FCSTD DOCUMENT  (FreeCAD 0.18.4R)
Label: keystone_3024_fp
License: Creative Commons Attribution
LicenseURL: http://creativecommons.org/licenses/by/4.0/
objects: Sketcher::SketchObject×4, App::Annotation×2
note: 4 computed .brp shape members not serialized (recipe doc carries the construction recipe); baked Part::Feature solids carry a one-line shape summary decoded from their .brp

FEATURE [App::Annotation] Text  label="Ref#_1.0mm"
  LabelText = REF**
  Position = (-9,-16,0)
FEATURE [App::Annotation] Text001  label="Value#_0.8mm"
  LabelText = Value 
  Position = (8,-16,0)
FEATURE [Sketcher::SketchObject] Sketch  label="F_Silks_0.16"
  sketch-geometry (57):
    g0: ArcOfCircle CenterX=6.39178 CenterY=-6.2773 CenterZ=0 NormalX=0 NormalY=0 NormalZ=1 AngleXU=0 Radius=2.3622 StartAngle=5.5152 EndAngle=6.28319
    g1: ArcOfCircle CenterX=6.39178 CenterY=6.27729 CenterZ=0 NormalX=0 NormalY=0 NormalZ=1 AngleXU=-3.14159 Radius=2.3622 StartAngle=2.48526 EndAngle=3.14159
    g2: LineSegment StartX=-2.54 StartY=-11.6713 StartZ=0 EndX=2.54 EndY=-11.6713 EndZ=0
    g3: LineSegment StartX=4.7117 StartY=-11.6713 StartZ=0 EndX=2.54 EndY=-11.6713 EndZ=0
    g4: LineSegment StartX=-2.54 StartY=-11.6713 StartZ=0 EndX=-4.7117 EndY=-11.6713 EndZ=0
    g5: LineSegment StartX=2.54 StartY=11.6713 StartZ=0 EndX=-2.54 EndY=11.6713 EndZ=0
    g6: LineSegment StartX=-2.54 StartY=11.6713 StartZ=0 EndX=-4.7117 EndY=11.6713 EndZ=0
    g7: LineSegment StartX=4.7117 StartY=11.6713 StartZ=0 EndX=2.54 EndY=11.6713 EndZ=0
    g8: LineSegment StartX=-11.5443 StartY=3.7846 StartZ=0 EndX=-4.7117 EndY=11.4173 EndZ=0
    g9: LineSegment StartX=-4.7117 StartY=-11.4173 StartZ=0 EndX=-11.5443 EndY=-3.7846 EndZ=0
    g10: LineSegment StartX=8.09093 StartY=-7.91829 StartZ=0 EndX=4.7117 EndY=-11.4173 EndZ=0
    g11: ArcOfCircle CenterX=6.39178 CenterY=-6.2773 CenterZ=0 NormalX=0 NormalY=0 NormalZ=1 AngleXU=0 Radius=2.3622 StartAngle=0 EndAngle=0.656334
    g12: ArcOfCircle CenterX=6.39178 CenterY=6.27729 CenterZ=0 NormalX=0 NormalY=0 NormalZ=1 AngleXU=-3.14159 Radius=2.3622 StartAngle=3.14159 EndAngle=3.90958
    g13: LineSegment StartX=4.7117 StartY=11.4173 StartZ=0 EndX=8.09093 EndY=7.91828 EndZ=0
    g14: BSplineCurve PolesCount=15 KnotsCount=15 Degree=1 IsPeriodic=0
    g15: BSplineCurve PolesCount=15 KnotsCount=15 Degree=1 IsPeriodic=0
    g16: LineSegment StartX=-12.0523 StartY=-3.7846 StartZ=0 EndX=-11.7983 EndY=-3.7846 EndZ=0
    g17: LineSegment StartX=-12.0523 StartY=3.7846 StartZ=0 EndX=-11.7983 EndY=3.7846 EndZ=0
    g18: LineSegment StartX=-12.0523 StartY=3.7846 StartZ=0 EndX=-12.0523 EndY=-3.7846 EndZ=0
    g19: LineSegment StartX=-11.7983 StartY=3.7846 StartZ=0 EndX=-11.7983 EndY=-3.7846 EndZ=0
    g20: BSplineCurve PolesCount=15 KnotsCount=15 Degree=1 IsPeriodic=0
    g21: BSplineCurve PolesCount=15 KnotsCount=15 Degree=1 IsPeriodic=0
    g22: BSplineCurve PolesCount=15 KnotsCount=15 Degree=1 IsPeriodic=0
    g23: BSplineCurve PolesCount=15 KnotsCount=15 Degree=1 IsPeriodic=0
    g24: LineSegment StartX=-11.5443 StartY=-3.7846 StartZ=0 EndX=-11.5443 EndY=3.7846 EndZ=0
    g25: LineSegment StartX=4.7117 StartY=-11.4173 StartZ=0 EndX=-4.7117 EndY=-11.4173 EndZ=0
    g26: LineSegment StartX=-4.7117 StartY=11.4173 StartZ=0 EndX=4.7117 EndY=11.4173 EndZ=0
    g27: LineSegment StartX=-11.7675 StartY=-3.6322 StartZ=0 EndX=-11.7675 EndY=3.6322 EndZ=0
    g28: LineSegment StartX=-12.0723 StartY=-3.683 StartZ=0 EndX=-12.0723 EndY=3.683 EndZ=0
    g29: LineSegment StartX=-7.43483 StartY=7.10236 StartZ=0 EndX=-10.1203 EndY=4.01304 EndZ=0
    g30: ArcOfCircle CenterX=-5.3921 CenterY=9.2456 CenterZ=0 NormalX=0 NormalY=0 NormalZ=1 AngleXU=0 Radius=2.3622 StartAngle=1.5708 EndAngle=2.35619
    g31: LineSegment StartX=-5.3921 StartY=11.6078 StartZ=0 EndX=4.7425 EndY=11.6078 EndZ=0
    g32: LineSegment StartX=4.7425 StartY=11.6078 StartZ=0 EndX=4.7425 EndY=10.9728 EndZ=0
    g33: LineSegment StartX=3.9297 StartY=10.16 StartZ=0 EndX=-0.725459 EndY=10.16 EndZ=0
    g34: ArcOfCircle CenterX=-0.725459 CenterY=1.27 CenterZ=0 NormalX=0 NormalY=0 NormalZ=1 AngleXU=0 Radius=8.89 StartAngle=1.5708 EndAngle=2.42601
    g35: ArcOfCircle CenterX=-9.5069 CenterY=3.4798 CenterZ=0 NormalX=0 NormalY=0 NormalZ=1 AngleXU=0 Radius=0.8128 StartAngle=2.42601 EndAngle=3.14159
    g36: LineSegment StartX=-10.3197 StartY=3.4798 StartZ=0 EndX=-10.3197 EndY=-3.4798 EndZ=0
    g37: ArcOfCircle CenterX=-9.5069 CenterY=-3.4798 CenterZ=0 NormalX=0 NormalY=0 NormalZ=1 AngleXU=0 Radius=0.8128 StartAngle=3.14159 EndAngle=3.85718
    g38: LineSegment StartX=-10.1203 StartY=-4.01305 StartZ=0 EndX=-7.43483 EndY=-7.10237 EndZ=0
    g39: ArcOfCircle CenterX=-0.725459 CenterY=-1.27 CenterZ=0 NormalX=0 NormalY=0 NormalZ=1 AngleXU=-3.14159 Radius=8.89 StartAngle=0.715585 EndAngle=1.5708
    g40: LineSegment StartX=-0.725459 StartY=-10.16 StartZ=0 EndX=3.9297 EndY=-10.16 EndZ=0
    g41: LineSegment StartX=4.7425 StartY=-10.9728 StartZ=0 EndX=4.7425 EndY=-11.6078 EndZ=0
    g42: LineSegment StartX=4.7425 StartY=-11.6078 StartZ=0 EndX=-5.3921 EndY=-11.6078 EndZ=0
    g43: ArcOfCircle CenterX=-5.3921 CenterY=-9.2456 CenterZ=0 NormalX=0 NormalY=0 NormalZ=1 AngleXU=0 Radius=2.3622 StartAngle=3.92699 EndAngle=4.71239
    g44: LineSegment StartX=-7.06243 StartY=-10.9159 StartZ=0 EndX=-13.282 EndY=-4.69632 EndZ=0
    g45: ArcOfCircle CenterX=-12.7073 CenterY=-4.12158 CenterZ=0 NormalX=0 NormalY=0 NormalZ=1 AngleXU=0 Radius=0.8128 StartAngle=3.14159 EndAngle=3.92699
    g46: LineSegment StartX=-13.5201 StartY=-4.12158 StartZ=0 EndX=-13.5201 EndY=-3.683 EndZ=0
    g47: LineSegment StartX=-13.5201 StartY=3.683 StartZ=0 EndX=-13.5201 EndY=-3.683 EndZ=0
    g48: LineSegment StartX=-13.5201 StartY=3.683 StartZ=0 EndX=-13.5201 EndY=4.12158 EndZ=0
    g49: ArcOfCircle CenterX=-12.7073 CenterY=4.12158 CenterZ=0 NormalX=0 NormalY=0 NormalZ=1 AngleXU=0 Radius=0.8128 StartAngle=2.35619 EndAngle=3.14159
    g50: LineSegment StartX=-13.282 StartY=4.69632 StartZ=0 EndX=-7.06243 EndY=10.9159 EndZ=0
    g51: LineSegment StartX=4.7425 StartY=-10.9728 StartZ=0 EndX=3.9297 EndY=-10.16 EndZ=0
    g52: LineSegment StartX=3.9297 StartY=10.16 StartZ=0 EndX=4.7425 EndY=10.9728 EndZ=0
    g53: LineSegment StartX=-12.0723 StartY=3.6322 StartZ=0 EndX=-11.7675 EndY=3.6322 EndZ=0
    g54: LineSegment StartX=-12.0723 StartY=-3.6322 StartZ=0 EndX=-11.7675 EndY=-3.6322 EndZ=0
    g55: LineSegment StartX=-13.5201 StartY=-3.683 StartZ=0 EndX=-12.0723 EndY=-3.683 EndZ=0
    g56: LineSegment StartX=-12.0723 StartY=3.683 StartZ=0 EndX=-13.5201 EndY=3.683 EndZ=0
FEATURE [Sketcher::SketchObject] Sketch011  label="Pads_TH_SMD"
  ExternalGeometry = -> [Sketch]
  sketch-geometry (9):
    g0: Circle CenterX=0 CenterY=0 CenterZ=0 NormalX=0 NormalY=0 NormalZ=1 AngleXU=0 Radius=8.255
    g1: LineSegment StartX=-2.54 StartY=17.0053 StartZ=0 EndX=2.54 EndY=17.0053 EndZ=0
    g2: LineSegment StartX=2.54 StartY=17.0053 StartZ=0 EndX=2.54 EndY=11.9253 EndZ=0
    g3: LineSegment StartX=2.54 StartY=11.9253 StartZ=0 EndX=-2.54 EndY=11.9253 EndZ=0
    g4: LineSegment StartX=-2.54 StartY=11.9253 StartZ=0 EndX=-2.54 EndY=17.0053 EndZ=0
    g5: LineSegment StartX=-2.54 StartY=-11.9253 StartZ=0 EndX=2.54 EndY=-11.9253 EndZ=0
    g6: LineSegment StartX=2.54 StartY=-11.9253 StartZ=0 EndX=2.54 EndY=-17.0053 EndZ=0
    g7: LineSegment StartX=2.54 StartY=-17.0053 StartZ=0 EndX=-2.54 EndY=-17.0053 EndZ=0
    g8: LineSegment StartX=-2.54 StartY=-17.0053 StartZ=0 EndX=-2.54 EndY=-11.9253 EndZ=0
FEATURE [Sketcher::SketchObject] Sketch012  label="F_CrtYd_0.05"
  sketch-geometry (44):
    g0: ArcOfCircle [constr] CenterX=6.39178 CenterY=-6.2773 CenterZ=0 NormalX=0 NormalY=0 NormalZ=1 AngleXU=0 Radius=2.3622 StartAngle=5.5152 EndAngle=6.28319
    g1: ArcOfCircle [constr] CenterX=6.39178 CenterY=6.27729 CenterZ=0 NormalX=0 NormalY=0 NormalZ=1 AngleXU=-3.14159 Radius=2.3622 StartAngle=2.48526 EndAngle=3.14159
    g2: LineSegment [constr] StartX=-2.54 StartY=-11.9253 StartZ=0 EndX=-4.7117 EndY=-11.9253 EndZ=0
    g3: LineSegment [constr] StartX=4.7117 StartY=-11.9253 StartZ=0 EndX=2.54 EndY=-11.9253 EndZ=0
    g4: LineSegment [constr] StartX=4.7117 StartY=11.9253 StartZ=0 EndX=2.54 EndY=11.9253 EndZ=0
    g5: LineSegment [constr] StartX=-2.54 StartY=11.9253 StartZ=0 EndX=-4.7117 EndY=11.9253 EndZ=0
    g6: LineSegment [constr] StartX=8.09093 StartY=-7.91829 StartZ=0 EndX=4.7117 EndY=-11.4173 EndZ=0
    g7: ArcOfCircle [constr] CenterX=6.39178 CenterY=-6.2773 CenterZ=0 NormalX=0 NormalY=0 NormalZ=1 AngleXU=0 Radius=2.3622 StartAngle=0 EndAngle=0.656334
    g8: ArcOfCircle [constr] CenterX=14.5415 CenterY=-2.36891e-06 CenterZ=0 NormalX=0 NormalY=0 NormalZ=1 AngleXU=-3.14159 Radius=7.9248 StartAngle=5.62685 EndAngle=6.93952
    g9: ArcOfCircle [constr] CenterX=6.39178 CenterY=6.27729 CenterZ=0 NormalX=0 NormalY=0 NormalZ=1 AngleXU=-3.14159 Radius=2.3622 StartAngle=3.14159 EndAngle=3.90958
    g10: LineSegment [constr] StartX=4.7117 StartY=11.4173 StartZ=0 EndX=8.09093 EndY=7.91828 EndZ=0
    g11: LineSegment [constr] StartX=-4.7117 StartY=11.9253 StartZ=0 EndX=-4.7117 EndY=11.6713 EndZ=0
    g12: LineSegment [constr] StartX=4.7117 StartY=11.9253 StartZ=0 EndX=4.7117 EndY=11.6713 EndZ=0
    g13: LineSegment [constr] StartX=2.54 StartY=17.0053 StartZ=0 EndX=2.54 EndY=12.1793 EndZ=0
    g14: LineSegment [constr] StartX=-2.54 StartY=12.1793 StartZ=0 EndX=-2.54 EndY=17.0053 EndZ=0
    g15: LineSegment [constr] StartX=-2.54 StartY=17.0053 StartZ=0 EndX=2.54 EndY=17.0053 EndZ=0
    g16: LineSegment [constr] StartX=4.7117 StartY=-11.9253 StartZ=0 EndX=4.7117 EndY=-11.6713 EndZ=0
    g17: LineSegment [constr] StartX=-4.7117 StartY=-11.9253 StartZ=0 EndX=-4.7117 EndY=-11.6713 EndZ=0
    g18: LineSegment [constr] StartX=2.54 StartY=-17.0053 StartZ=0 EndX=2.54 EndY=-12.1793 EndZ=0
    g19: LineSegment [constr] StartX=-2.54 StartY=-12.1793 StartZ=0 EndX=-2.54 EndY=-17.0053 EndZ=0
    g20: LineSegment [constr] StartX=-2.54 StartY=-17.0053 StartZ=0 EndX=2.54 EndY=-17.0053 EndZ=0
    g21: ArcOfCircle [constr] CenterX=-5.3921 CenterY=9.2456 CenterZ=0 NormalX=0 NormalY=0 NormalZ=1 AngleXU=0 Radius=2.3622 StartAngle=1.5708 EndAngle=2.35619
    g22: ArcOfCircle [constr] CenterX=-5.3921 CenterY=-9.2456 CenterZ=0 NormalX=0 NormalY=0 NormalZ=1 AngleXU=0 Radius=2.3622 StartAngle=3.92699 EndAngle=4.71239
    g23: LineSegment [constr] StartX=-7.06243 StartY=-10.9159 StartZ=0 EndX=-13.282 EndY=-4.69632 EndZ=0
    g24: ArcOfCircle [constr] CenterX=-12.7073 CenterY=-4.12158 CenterZ=0 NormalX=0 NormalY=0 NormalZ=1 AngleXU=0 Radius=0.8128 StartAngle=3.14159 EndAngle=3.92699
    g25: LineSegment [constr] StartX=-13.5201 StartY=-4.12158 StartZ=0 EndX=-13.5201 EndY=-3.683 EndZ=0
    g26: LineSegment [constr] StartX=-13.5201 StartY=3.683 StartZ=0 EndX=-13.5201 EndY=-3.683 EndZ=0
    g27: LineSegment [constr] StartX=-13.5201 StartY=3.683 StartZ=0 EndX=-13.5201 EndY=4.12158 EndZ=0
    g28: ArcOfCircle [constr] CenterX=-12.7073 CenterY=4.12158 CenterZ=0 NormalX=0 NormalY=0 NormalZ=1 AngleXU=0 Radius=0.8128 StartAngle=2.35619 EndAngle=3.14159
    g29: LineSegment [constr] StartX=-13.282 StartY=4.69632 StartZ=0 EndX=-7.06243 EndY=10.9159 EndZ=0
    g30: LineSegment StartX=-3.048 StartY=17.5133 StartZ=0 EndX=3.048 EndY=17.5133 EndZ=0
    g31: LineSegment StartX=3.048 StartY=17.5133 StartZ=0 EndX=3.048 EndY=12.4333 EndZ=0
    g32: LineSegment StartX=3.048 StartY=12.4333 StartZ=0 EndX=9.26198 EndY=12.4333 EndZ=0
    g33: LineSegment StartX=9.26198 StartY=12.4333 StartZ=0 EndX=9.26198 EndY=-12.4333 EndZ=0
    g34: LineSegment StartX=9.26198 StartY=-12.4333 StartZ=0 EndX=3.048 EndY=-12.4333 EndZ=0
    g35: LineSegment StartX=3.048 StartY=-12.4333 StartZ=0 EndX=3.048 EndY=-17.5133 EndZ=0
    g36: LineSegment StartX=3.048 StartY=-17.5133 StartZ=0 EndX=-3.048 EndY=-17.5133 EndZ=0
    g37: LineSegment StartX=-3.048 StartY=-17.5133 StartZ=0 EndX=-3.048 EndY=-12.4333 EndZ=0
    g38: LineSegment StartX=-3.048 StartY=-12.4333 StartZ=0 EndX=-6.9288 EndY=-12.4333 EndZ=0
    g39: LineSegment StartX=-6.9288 StartY=-12.4333 StartZ=0 EndX=-14.0281 EndY=-5.334 EndZ=0
    g40: LineSegment StartX=-14.0281 StartY=-5.334 StartZ=0 EndX=-14.0281 EndY=5.334 EndZ=0
    g41: LineSegment StartX=-14.0281 StartY=5.334 StartZ=0 EndX=-6.92881 EndY=12.4333 EndZ=0
    g42: LineSegment StartX=-6.92881 StartY=12.4333 StartZ=0 EndX=-3.048 EndY=12.4333 EndZ=0
    g43: LineSegment StartX=-3.048 StartY=12.4333 StartZ=0 EndX=-3.048 EndY=17.5133 EndZ=0
  constraints (71):
    c: Block(g29)
    c: Block(g21)
    c: Block(g11)
    c: Block(g5)
    c: Block(g14)
    c: Block(g15)
    c: Block(g13)
    c: Block(g4)
    c: Block(g12)
    c: Block(g10)
    c: Block(g9)
    c: Block(g1)
    c: Block(g8)
    c: Block(g7)
    c: Block(g0)
    c: Block(g6)
    c: Block(g16)
    c: Block(g3)
    c: Block(g18)
    c: Block(g20)
    c: Block(g19)
    c: Block(g2)
    c: Block(g17)
    c: Block(g22)
    c: Block(g23)
    c: Block(g24)
    c: Block(g25)
    c: Block(g26)
    c: Block(g27)
    c: Block(g28)
    c: Coincident(g30,g31)
    c: Coincident(g32,g33)
    c: Coincident(g33,g34)
    c: Coincident(g34,g35)
    c: Coincident(g35,g36)
    c: Coincident(g36,g37)
    c: Coincident(g37,g38)
    c: Coincident(g38,g39)
    c: Coincident(g39,g40)
    c: Coincident(g40,g41)
    c: Coincident(g41,g42)
    c: Coincident(g42,g43)
    c: Coincident(g43,g30)
    c: Vertical(g43)
    c: Horizontal(g30)
    c: Vertical(g31)
    c: Coincident(g31,g32)
    c: Horizontal(g32)
    c: Vertical(g33)
    c: Horizontal(g34)
    c: Vertical(g35)
    c: Horizontal(g36)
    c: Vertical(g37)
    c: Horizontal(g38)
    c: Horizontal(g42)
    c: DistanceY(g14,g30) = 0.508
    c: DistanceX(g13,g30) = 0.508
    c: DistanceY(g4,g31) = 0.508
    c: Distance(g1,g33) = 0.508
    c: DistanceY(g34,g3) = 0.508
    c: DistanceX(g18,g35) = 0.508
    c: DistanceY(g36,g19) = 0.508
    c: DistanceX(g37,g2) = 0.508
    c: DistanceY(g38,g2) = 0.508
    c: DistanceX(g39,g25) = 0.508
    c: DistanceY(g5,g42) = 0.508
    c: Parallel(g39,g23)
    c: Symmetric(g40,g39,g-1)
    c: DistanceX(g30,g14) = 0.508
    c: Parallel(g41,g29)
    c: DistanceY(g40,g40) = 10.668
FEATURE [Sketcher::SketchObject] Sketch013  label="F_Fab_0.1"
  sketch-geometry (114):
    g0: ArcOfCircle CenterX=-3.64238e-06 CenterY=-14.4653 CenterZ=0 NormalX=0 NormalY=0 NormalZ=1 AngleXU=1.5708 Radius=1.1811 StartAngle=3.14159 EndAngle=6.28319
    g1: ArcOfCircle CenterX=-3.01597 CenterY=-6.0198 CenterZ=0 NormalX=0 NormalY=0 NormalZ=1 AngleXU=3.14159 Radius=1.5875 StartAngle=0 EndAngle=1.39167
    g2: ArcOfCircle CenterX=-3.64238e-06 CenterY=14.4653 CenterZ=0 NormalX=0 NormalY=0 NormalZ=1 AngleXU=-1.5708 Radius=1.1811 StartAngle=0 EndAngle=3.14159
    g3: ArcOfCircle CenterX=-3.01597 CenterY=6.0198 CenterZ=0 NormalX=0 NormalY=0 NormalZ=1 AngleXU=-3.14159 Radius=1.5875 StartAngle=0 EndAngle=1.39167
    g4: ArcOfCircle CenterX=6.39178 CenterY=-6.2773 CenterZ=0 NormalX=0 NormalY=0 NormalZ=1 AngleXU=0 Radius=2.3622 StartAngle=5.5152 EndAngle=6.28319
    g5: ArcOfCircle CenterX=6.39178 CenterY=6.27729 CenterZ=0 NormalX=0 NormalY=0 NormalZ=1 AngleXU=-3.14159 Radius=2.3622 StartAngle=2.48526 EndAngle=3.14159
    g6: LineSegment StartX=-2.54 StartY=-11.9253 StartZ=0 EndX=-4.7117 EndY=-11.9253 EndZ=0
    g7: LineSegment StartX=4.7117 StartY=-11.9253 StartZ=0 EndX=2.54 EndY=-11.9253 EndZ=0
    g8: LineSegment StartX=-2.54 StartY=-11.6713 StartZ=0 EndX=2.54 EndY=-11.6713 EndZ=0
    g9: LineSegment StartX=4.7117 StartY=-11.6713 StartZ=0 EndX=2.54 EndY=-11.6713 EndZ=0
    g10: LineSegment StartX=-2.54 StartY=-11.6713 StartZ=0 EndX=-4.7117 EndY=-11.6713 EndZ=0
    g11: LineSegment StartX=4.6609 StartY=-4.4323 StartZ=0 EndX=4.6609 EndY=-4.4577 EndZ=0
    g12: LineSegment StartX=4.7117 StartY=11.9253 StartZ=0 EndX=2.54 EndY=11.9253 EndZ=0
    g13: LineSegment StartX=-2.54 StartY=11.9253 StartZ=0 EndX=-4.7117 EndY=11.9253 EndZ=0
    g14: LineSegment StartX=2.54 StartY=11.6713 StartZ=0 EndX=-2.54 EndY=11.6713 EndZ=0
    g15: LineSegment StartX=-2.54 StartY=11.6713 StartZ=0 EndX=-4.7117 EndY=11.6713 EndZ=0
    g16: LineSegment StartX=4.7117 StartY=11.6713 StartZ=0 EndX=2.54 EndY=11.6713 EndZ=0
    g17: LineSegment StartX=4.6609 StartY=7.6073 StartZ=0 EndX=4.6609 EndY=7.5819 EndZ=0
    g18: LineSegment StartX=4.6609 StartY=-7.6073 StartZ=0 EndX=-0.791825 EndY=-7.6073 EndZ=0
    g19: ArcOfCircle CenterX=-3.4163 CenterY=-6.0325 CenterZ=0 NormalX=0 NormalY=0 NormalZ=1 AngleXU=0 Radius=3.0607 StartAngle=0.550158 EndAngle=5.74273
    g20: LineSegment StartX=-0.807234 StartY=-4.4323 StartZ=0 EndX=4.6609 EndY=-4.4323 EndZ=0
    g21: LineSegment StartX=4.6609 StartY=-4.4577 StartZ=0 EndX=4.6609 EndY=-7.5819 EndZ=0
    g22: LineSegment StartX=4.6609 StartY=-7.5819 StartZ=0 EndX=4.6609 EndY=-7.6073 EndZ=0
    g23: LineSegment StartX=-11.5443 StartY=3.7846 StartZ=0 EndX=-4.7117 EndY=11.4173 EndZ=0
    g24: LineSegment StartX=-4.7117 StartY=-11.4173 StartZ=0 EndX=-11.5443 EndY=-3.7846 EndZ=0
    g25: LineSegment StartX=8.09093 StartY=-7.91829 StartZ=0 EndX=4.7117 EndY=-11.4173 EndZ=0
    g26: ArcOfCircle CenterX=6.39178 CenterY=-6.2773 CenterZ=0 NormalX=0 NormalY=0 NormalZ=1 AngleXU=0 Radius=2.3622 StartAngle=0 EndAngle=0.656334
    g27: ArcOfCircle CenterX=14.5415 CenterY=-2.36891e-06 CenterZ=0 NormalX=0 NormalY=0 NormalZ=1 AngleXU=-3.14159 Radius=7.9248 StartAngle=5.62685 EndAngle=6.93952
    g28: ArcOfCircle CenterX=6.39178 CenterY=6.27729 CenterZ=0 NormalX=0 NormalY=0 NormalZ=1 AngleXU=-3.14159 Radius=2.3622 StartAngle=3.14159 EndAngle=3.90958
    g29: LineSegment StartX=4.7117 StartY=11.4173 StartZ=0 EndX=8.09093 EndY=7.91828 EndZ=0
    g30: ArcOfCircle CenterX=-3.4163 CenterY=6.0325 CenterZ=0 NormalX=0 NormalY=0 NormalZ=1 AngleXU=-3.14159 Radius=3.0607 StartAngle=3.68204 EndAngle=8.87462
    g31: LineSegment StartX=-0.791825 StartY=7.6073 StartZ=0 EndX=4.6609 EndY=7.6073 EndZ=0
    g32: LineSegment StartX=4.6609 StartY=4.4577 StartZ=0 EndX=4.6609 EndY=7.5819 EndZ=0
    g33: LineSegment StartX=4.6609 StartY=4.4577 StartZ=0 EndX=4.6609 EndY=4.4323 EndZ=0
    g34: LineSegment StartX=4.6609 StartY=4.4323 StartZ=0 EndX=-0.807234 EndY=4.4323 EndZ=0
    g35: BSplineCurve PolesCount=15 KnotsCount=15 Degree=1 IsPeriodic=0
    g36: BSplineCurve PolesCount=15 KnotsCount=15 Degree=1 IsPeriodic=0
    g37: LineSegment StartX=-12.0523 StartY=-3.7846 StartZ=0 EndX=-11.7983 EndY=-3.7846 EndZ=0
    g38: LineSegment StartX=-12.0523 StartY=3.7846 StartZ=0 EndX=-11.7983 EndY=3.7846 EndZ=0
    g39: LineSegment StartX=-12.0523 StartY=3.7846 StartZ=0 EndX=-12.0523 EndY=-3.7846 EndZ=0
    g40: LineSegment StartX=-11.7983 StartY=3.7846 StartZ=0 EndX=-11.7983 EndY=-3.7846 EndZ=0
    g41: BSplineCurve PolesCount=15 KnotsCount=15 Degree=1 IsPeriodic=0
    g42: BSplineCurve PolesCount=15 KnotsCount=15 Degree=1 IsPeriodic=0
    g43: LineSegment StartX=-4.7117 StartY=11.9253 StartZ=0 EndX=-4.7117 EndY=11.6713 EndZ=0
    g44: LineSegment StartX=4.7117 StartY=11.9253 StartZ=0 EndX=4.7117 EndY=11.6713 EndZ=0
    g45: LineSegment StartX=4.6609 StartY=7.5819 StartZ=0 EndX=-1.23107 EndY=7.5819 EndZ=0
    g46: LineSegment StartX=-1.23107 StartY=4.4577 StartZ=0 EndX=4.6609 EndY=4.4577 EndZ=0
    g47: BSplineCurve PolesCount=15 KnotsCount=15 Degree=1 IsPeriodic=0
    g48: BSplineCurve PolesCount=15 KnotsCount=15 Degree=1 IsPeriodic=0
    g49: LineSegment StartX=-3.29882 StartY=7.5819 StartZ=0 EndX=-1.33032 EndY=7.5819 EndZ=0
    g50: ArcOfCircle CenterX=-3.01597 CenterY=6.0198 CenterZ=0 NormalX=0 NormalY=0 NormalZ=1 AngleXU=-3.14159 Radius=1.5875 StartAngle=4.89151 EndAngle=6.28319
    g51: LineSegment StartX=-1.33032 StartY=4.4577 StartZ=0 EndX=-3.29882 EndY=4.4577 EndZ=0
    g52: BSplineCurve PolesCount=15 KnotsCount=15 Degree=1 IsPeriodic=0
    g53: BSplineCurve PolesCount=15 KnotsCount=15 Degree=1 IsPeriodic=0
    g54: LineSegment StartX=2.54 StartY=17.0053 StartZ=0 EndX=2.54 EndY=12.1793 EndZ=0
    g55: LineSegment StartX=-2.54 StartY=12.1793 StartZ=0 EndX=-2.54 EndY=17.0053 EndZ=0
    g56: ArcOfCircle CenterX=-3.64238e-06 CenterY=14.4653 CenterZ=0 NormalX=0 NormalY=0 NormalZ=1 AngleXU=-1.5708 Radius=1.1811 StartAngle=3.14159 EndAngle=6.28319
    g57: LineSegment StartX=-2.54 StartY=17.0053 StartZ=0 EndX=2.54 EndY=17.0053 EndZ=0
    g58: BSplineCurve PolesCount=15 KnotsCount=15 Degree=1 IsPeriodic=0
    g59: BSplineCurve PolesCount=15 KnotsCount=15 Degree=1 IsPeriodic=0
    g60: LineSegment StartX=4.7117 StartY=-11.9253 StartZ=0 EndX=4.7117 EndY=-11.6713 EndZ=0
    g61: LineSegment StartX=-4.7117 StartY=-11.9253 StartZ=0 EndX=-4.7117 EndY=-11.6713 EndZ=0
    g62: LineSegment StartX=4.6609 StartY=-7.5819 StartZ=0 EndX=-1.23107 EndY=-7.5819 EndZ=0
    g63: LineSegment StartX=-1.23107 StartY=-4.4577 StartZ=0 EndX=4.6609 EndY=-4.4577 EndZ=0
    g64: BSplineCurve PolesCount=15 KnotsCount=15 Degree=1 IsPeriodic=0
    g65: BSplineCurve PolesCount=15 KnotsCount=15 Degree=1 IsPeriodic=0
    g66: LineSegment StartX=-1.33032 StartY=-4.4577 StartZ=0 EndX=-3.29882 EndY=-4.4577 EndZ=0
    g67: ArcOfCircle CenterX=-3.01597 CenterY=-6.0198 CenterZ=0 NormalX=0 NormalY=0 NormalZ=1 AngleXU=3.14159 Radius=1.5875 StartAngle=4.89151 EndAngle=6.28319
    g68: LineSegment StartX=-3.29882 StartY=-7.5819 StartZ=0 EndX=-1.33032 EndY=-7.5819 EndZ=0
    g69: BSplineCurve PolesCount=15 KnotsCount=15 Degree=1 IsPeriodic=0
    g70: BSplineCurve PolesCount=15 KnotsCount=15 Degree=1 IsPeriodic=0
    g71: ArcOfCircle CenterX=-3.64238e-06 CenterY=-14.4653 CenterZ=0 NormalX=0 NormalY=0 NormalZ=1 AngleXU=1.5708 Radius=1.1811 StartAngle=0 EndAngle=3.14159
    g72: LineSegment StartX=2.54 StartY=-17.0053 StartZ=0 EndX=2.54 EndY=-12.1793 EndZ=0
    g73: LineSegment StartX=-2.54 StartY=-12.1793 StartZ=0 EndX=-2.54 EndY=-17.0053 EndZ=0
    g74: LineSegment StartX=-2.54 StartY=-17.0053 StartZ=0 EndX=2.54 EndY=-17.0053 EndZ=0
    g75: LineSegment StartX=-11.5443 StartY=-3.7846 StartZ=0 EndX=-11.5443 EndY=3.7846 EndZ=0
    g76: LineSegment StartX=4.7117 StartY=-11.4173 StartZ=0 EndX=-4.7117 EndY=-11.4173 EndZ=0
    g77: LineSegment StartX=-4.7117 StartY=11.4173 StartZ=0 EndX=4.7117 EndY=11.4173 EndZ=0
    g78: LineSegment StartX=-1.23107 StartY=7.5819 StartZ=0 EndX=-1.23107 EndY=4.4577 EndZ=0
    g79: LineSegment StartX=-1.33032 StartY=7.5819 StartZ=0 EndX=-1.33032 EndY=4.4577 EndZ=0
    g80: LineSegment StartX=-2.54 StartY=12.1793 StartZ=0 EndX=2.54 EndY=12.1793 EndZ=0
    g81: LineSegment StartX=-1.23107 StartY=-7.5819 StartZ=0 EndX=-1.23107 EndY=-4.4577 EndZ=0
    g82: LineSegment StartX=-1.33032 StartY=-7.5819 StartZ=0 EndX=-1.33032 EndY=-4.4577 EndZ=0
    g83: LineSegment StartX=2.54 StartY=-12.1793 StartZ=0 EndX=-2.54 EndY=-12.1793 EndZ=0
    g84: LineSegment StartX=-11.7675 StartY=-3.6322 StartZ=0 EndX=-11.7675 EndY=3.6322 EndZ=0
    g85: LineSegment StartX=-12.0723 StartY=-3.683 StartZ=0 EndX=-12.0723 EndY=3.683 EndZ=0
    g86: LineSegment StartX=-7.43483 StartY=7.10236 StartZ=0 EndX=-10.1203 EndY=4.01304 EndZ=0
    g87: ArcOfCircle CenterX=-5.3921 CenterY=9.2456 CenterZ=0 NormalX=0 NormalY=0 NormalZ=1 AngleXU=0 Radius=2.3622 StartAngle=1.5708 EndAngle=2.35619
    g88: LineSegment StartX=-5.3921 StartY=11.6078 StartZ=0 EndX=4.7425 EndY=11.6078 EndZ=0
    g89: LineSegment StartX=4.7425 StartY=11.6078 StartZ=0 EndX=4.7425 EndY=10.9728 EndZ=0
    g90: LineSegment StartX=3.9297 StartY=10.16 StartZ=0 EndX=-0.725459 EndY=10.16 EndZ=0
    g91: ArcOfCircle CenterX=-0.725459 CenterY=1.27 CenterZ=0 NormalX=0 NormalY=0 NormalZ=1 AngleXU=0 Radius=8.89 StartAngle=1.5708 EndAngle=2.42601
    g92: ArcOfCircle CenterX=-9.5069 CenterY=3.4798 CenterZ=0 NormalX=0 NormalY=0 NormalZ=1 AngleXU=0 Radius=0.8128 StartAngle=2.42601 EndAngle=3.14159
    g93: LineSegment StartX=-10.3197 StartY=3.4798 StartZ=0 EndX=-10.3197 EndY=-3.4798 EndZ=0
    g94: ArcOfCircle CenterX=-9.5069 CenterY=-3.4798 CenterZ=0 NormalX=0 NormalY=0 NormalZ=1 AngleXU=0 Radius=0.8128 StartAngle=3.14159 EndAngle=3.85718
    g95: LineSegment StartX=-10.1203 StartY=-4.01305 StartZ=0 EndX=-7.43483 EndY=-7.10237 EndZ=0
    g96: ArcOfCircle CenterX=-0.725459 CenterY=-1.27 CenterZ=0 NormalX=0 NormalY=0 NormalZ=1 AngleXU=-3.14159 Radius=8.89 StartAngle=0.715585 EndAngle=1.5708
    g97: LineSegment StartX=-0.725459 StartY=-10.16 StartZ=0 EndX=3.9297 EndY=-10.16 EndZ=0
    g98: LineSegment StartX=4.7425 StartY=-10.9728 StartZ=0 EndX=4.7425 EndY=-11.6078 EndZ=0
    g99: LineSegment StartX=4.7425 StartY=-11.6078 StartZ=0 EndX=-5.3921 EndY=-11.6078 EndZ=0
    g100: ArcOfCircle CenterX=-5.3921 CenterY=-9.2456 CenterZ=0 NormalX=0 NormalY=0 NormalZ=1 AngleXU=0 Radius=2.3622 StartAngle=3.92699 EndAngle=4.71239
    g101: LineSegment StartX=-7.06243 StartY=-10.9159 StartZ=0 EndX=-13.282 EndY=-4.69632 EndZ=0
    g102: ArcOfCircle CenterX=-12.7073 CenterY=-4.12158 CenterZ=0 NormalX=0 NormalY=0 NormalZ=1 AngleXU=0 Radius=0.8128 StartAngle=3.14159 EndAngle=3.92699
    g103: LineSegment StartX=-13.5201 StartY=-4.12158 StartZ=0 EndX=-13.5201 EndY=-3.683 EndZ=0
    g104: LineSegment StartX=-13.5201 StartY=3.683 StartZ=0 EndX=-13.5201 EndY=-3.683 EndZ=0
    g105: LineSegment StartX=-13.5201 StartY=3.683 StartZ=0 EndX=-13.5201 EndY=4.12158 EndZ=0
    g106: ArcOfCircle CenterX=-12.7073 CenterY=4.12158 CenterZ=0 NormalX=0 NormalY=0 NormalZ=1 AngleXU=0 Radius=0.8128 StartAngle=2.35619 EndAngle=3.14159
    g107: LineSegment StartX=-13.282 StartY=4.69632 StartZ=0 EndX=-7.06243 EndY=10.9159 EndZ=0
    g108: LineSegment StartX=4.7425 StartY=-10.9728 StartZ=0 EndX=3.9297 EndY=-10.16 EndZ=0
    g109: LineSegment StartX=3.9297 StartY=10.16 StartZ=0 EndX=4.7425 EndY=10.9728 EndZ=0
    g110: LineSegment StartX=-12.0723 StartY=3.6322 StartZ=0 EndX=-11.7675 EndY=3.6322 EndZ=0
    g111: LineSegment StartX=-12.0723 StartY=-3.6322 StartZ=0 EndX=-11.7675 EndY=-3.6322 EndZ=0
    g112: LineSegment StartX=-13.5201 StartY=-3.683 StartZ=0 EndX=-12.0723 EndY=-3.683 EndZ=0
    g113: LineSegment StartX=-12.0723 StartY=3.683 StartZ=0 EndX=-13.5201 EndY=3.683 EndZ=0
